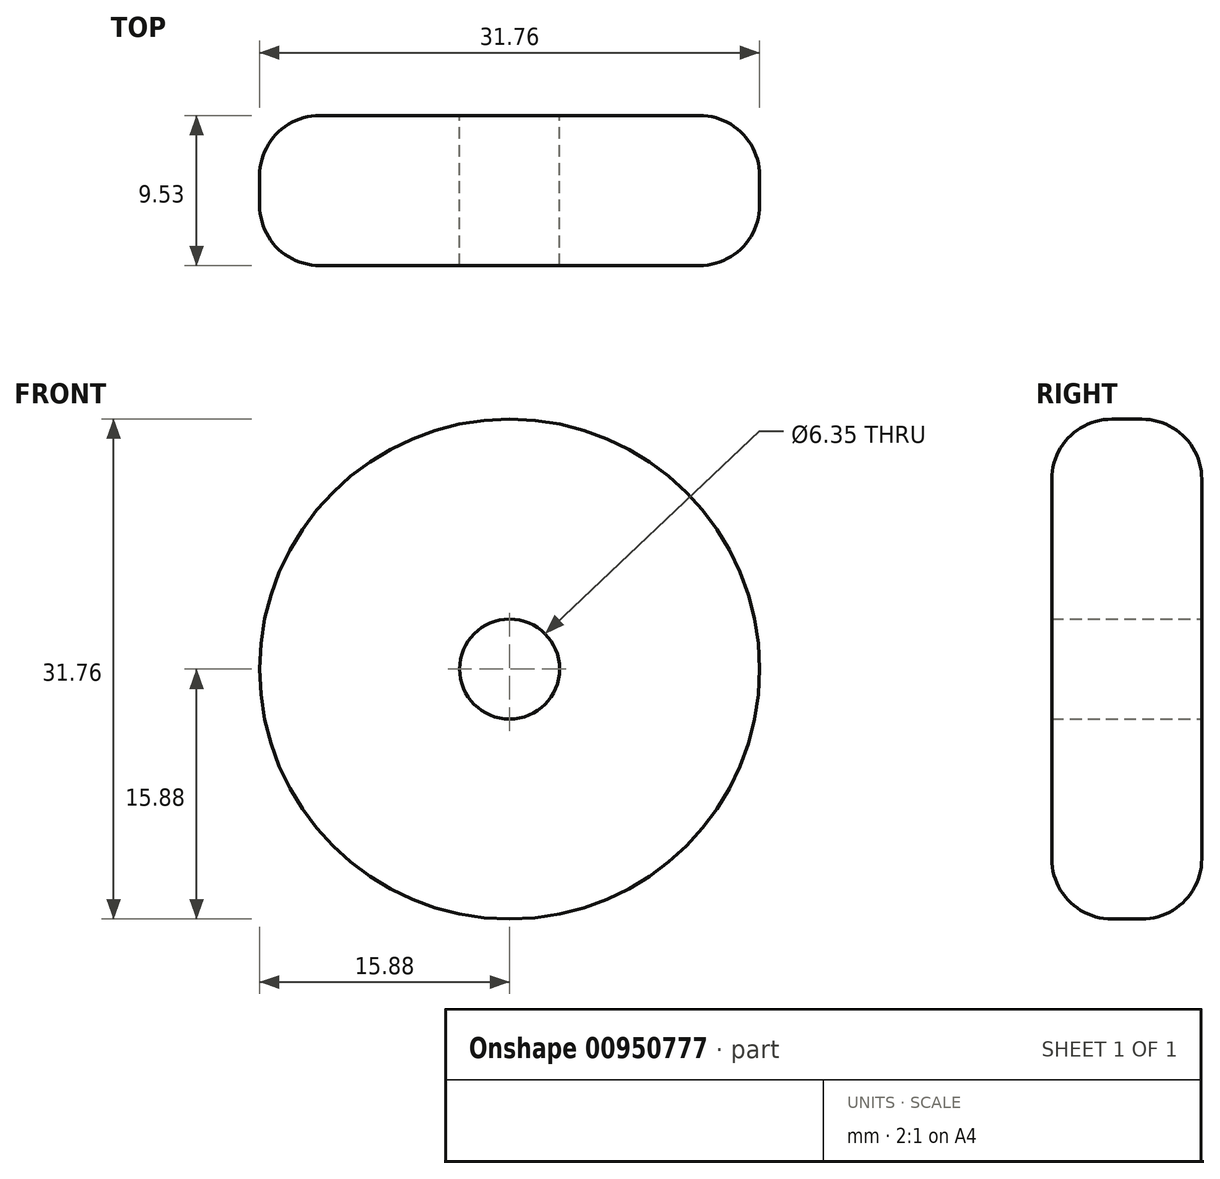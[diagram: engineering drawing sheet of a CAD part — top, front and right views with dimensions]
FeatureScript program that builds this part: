
annotation { "Feature Type Name" : "Feature", "Feature Type Description" : "" }
export const myFeature = defineFeature(function(context is Context, id is Id, definition is map)
    precondition{}
    {
        {
            var Q0;
            Q0=qCreatedBy(makeId("Front.planeOp"),FACE);
            var sketch = newSketch(context, id + "F0", { "sketchPlane" : qUnion([Q0])});
            skPoint(sketch, "E0", {"position": v(0, 0) * mm});
            skLineSegment(sketch, "E1", {"start": v(0, 0) * mm, "end": v(-15.87, 0) * mm});
            skLineSegment(sketch, "E2", {"start": v(0, 0) * mm, "end": v(0, -3.17) * mm});
            skCircle(sketch, "E3", {"center": v(0, 0) * mm, "radius": 3.17 * mm});
            skCircle(sketch, "E4", {"center": v(0, 0) * mm, "radius": 15.87 * mm});
            skSolve(sketch);
        }
        {
            var Q0;
            Q0=makeQuery(id+"F0.imprint","IMPRINT",FACE,{"disambiguationData":[TD([[makeQuery(id+"F0.imprint","IMPRINT",EDGE,{"derivedFrom":sQuery(id+"F0.wireOp",EDGE,"E4")}),1.0]])]});
            extrude(context, id + "F1", {"entities" : qUnion([Q0]), "depth" : 9.52 * mm, "offsetDistance" : 25.4 * mm});
        }
        {
            var Q0;
            Q0=makeQuery(id+"F1.opExtrude","CAP_EDGE",EDGE,{"disambiguationData":[OSD([sQuery(id+"F0.wireOp",EDGE,"E4")])],"isStart":false});
            var Q1;
            Q1=makeQuery(id+"F1.opExtrude","CAP_EDGE",EDGE,{"disambiguationData":[OSD([sQuery(id+"F0.wireOp",EDGE,"E4")])],"isStart":true});
            fillet(context, id + "F2", {"entities" : qUnion([Q0, Q1]), "radius" : 3.8 * mm, "tangentPropagation" : true, "allowEdgeOverflow" : false});
        }
    });
